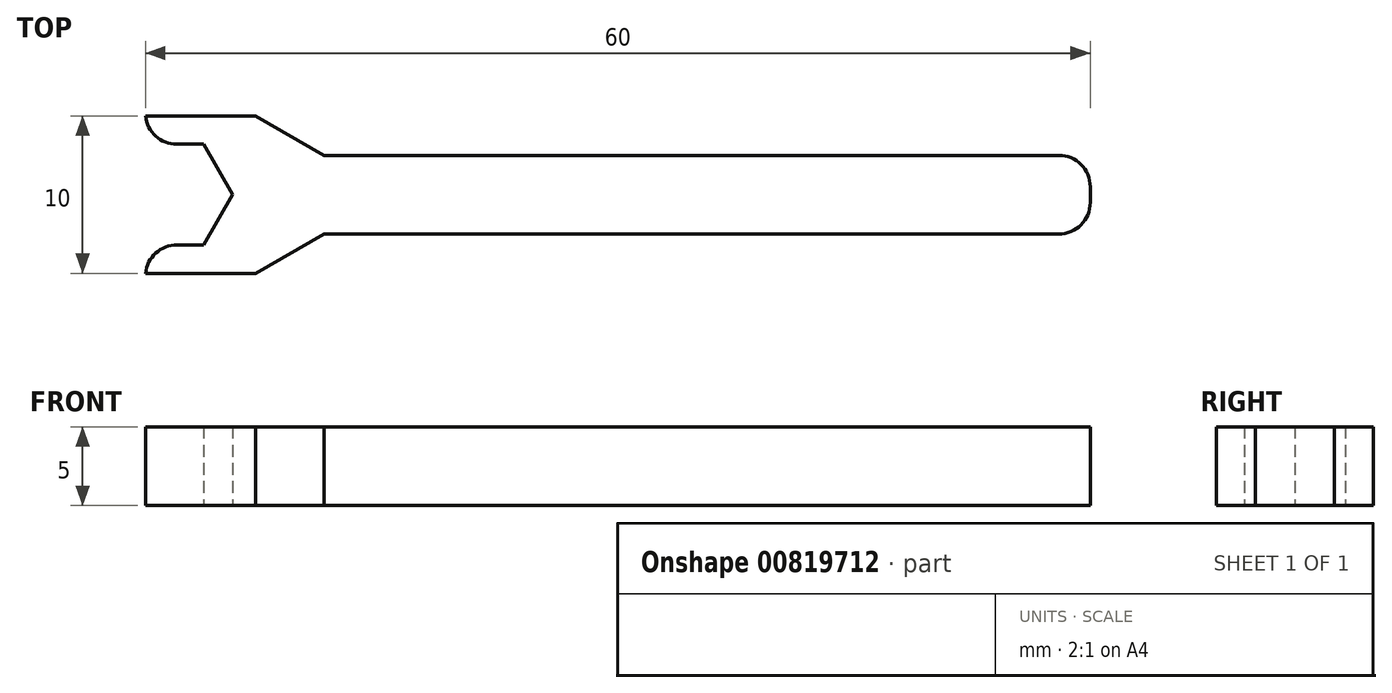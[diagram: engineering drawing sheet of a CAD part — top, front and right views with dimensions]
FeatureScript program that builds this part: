
annotation { "Feature Type Name" : "Feature", "Feature Type Description" : "" }
export const myFeature = defineFeature(function(context is Context, id is Id, definition is map)
    precondition{}
    {
        {
            var Q0;
            Q0=qCreatedBy(makeId("Top.planeOp"),FACE);
            var sketch = newSketch(context, id + "F0", { "sketchPlane" : qUnion([Q0])});
            skCircle(sketch, "E0.cCircle", {"center": v(0, 0) * mm, "radius": 3.2 * mm, "construction": true});
            skLineSegment(sketch, "E0.0", {"start": v(3.7, 0) * mm, "end": v(1.85, -3.2) * mm});
            skLineSegment(sketch, "E0.1", {"start": v(1.85, -3.2) * mm, "end": v(-1.85, -3.2) * mm});
            skLineSegment(sketch, "E0.2", {"start": v(-1.85, -3.2) * mm, "end": v(-3.7, 0) * mm, "construction": true});
            skLineSegment(sketch, "E0.3", {"start": v(-3.7, 0) * mm, "end": v(-1.85, 3.2) * mm, "construction": true});
            skLineSegment(sketch, "E0.4", {"start": v(-1.85, 3.2) * mm, "end": v(1.85, 3.2) * mm});
            skLineSegment(sketch, "E0.5", {"start": v(1.85, 3.2) * mm, "end": v(3.7, 0) * mm});
            skPoint(sketch, "E0.0.midPoint", {"position": v(2.77, -1.6) * mm});
            skLineSegment(sketch, "E1", {"start": v(-1.85, 3.2) * mm, "end": v(-1.85, 5) * mm});
            skLineSegment(sketch, "E2", {"start": v(-1.85, 5) * mm, "end": v(5.15, 5) * mm});
            skLineSegment(sketch, "E3", {"start": v(5.15, 5) * mm, "end": v(9.48, 2.5) * mm});
            skLineSegment(sketch, "E4", {"start": v(9.48, 2.5) * mm, "end": v(58.15, 2.5) * mm});
            skLineSegment(sketch, "E5", {"start": v(-4.42, 0) * mm, "end": v(61.3, 0) * mm, "construction": true});
            skLineSegment(sketch, "E6.MirrorCS", {"start": v(9.48, -2.5) * mm, "end": v(58.15, -2.5) * mm});
            skLineSegment(sketch, "E7.MirrorCS", {"start": v(-1.85, -5) * mm, "end": v(5.15, -5) * mm});
            skLineSegment(sketch, "E8.MirrorCS", {"start": v(-1.85, -3.2) * mm, "end": v(-1.85, -5) * mm});
            skLineSegment(sketch, "E9.MirrorCS", {"start": v(5.15, -5) * mm, "end": v(9.48, -2.5) * mm});
            skLineSegment(sketch, "E10", {"start": v(58.15, -2.5) * mm, "end": v(58.15, 2.5) * mm});
            skSolve(sketch);
        }
        {
            var Q0;
            Q0 = qSketchRegion(id + "F0", true);
            extrude(context, id + "F1", {"entities" : qUnion([Q0]), "endBound" : BoundingType.SYMMETRIC, "depth" : 5 * mm, "offsetDistance" : 25 * mm});
        }
        {
            var Q0;
            Q0=makeQuery(id+"F1.opExtrude","SWEPT_EDGE",EDGE,{"disambiguationData":[OSD([sQuery(id+"F0.wireOp",EDGE,"E0.4"),sQuery(id+"F0.wireOp",EDGE,"E1")])]});
            var Q1;
            Q1=makeQuery(id+"F1.opExtrude","SWEPT_EDGE",EDGE,{"disambiguationData":[OSD([sQuery(id+"F0.wireOp",EDGE,"E0.1"),sQuery(id+"F0.wireOp",EDGE,"E8.MirrorCS")])]});
            var Q2;
            Q2=makeQuery(id+"F1.opExtrude","SWEPT_EDGE",EDGE,{"disambiguationData":[OSD([sQuery(id+"F0.wireOp",EDGE,"E6.MirrorCS"),sQuery(id+"F0.wireOp",EDGE,"E10")])]});
            var Q3;
            Q3=makeQuery(id+"F1.opExtrude","SWEPT_EDGE",EDGE,{"disambiguationData":[OSD([sQuery(id+"F0.wireOp",EDGE,"E4"),sQuery(id+"F0.wireOp",EDGE,"E10")])]});
            fillet(context, id + "F2", {"entities" : qUnion([Q0, Q1, Q2, Q3]), "radius" : 2 * mm, "tangentPropagation" : true, "allowEdgeOverflow" : false});
        }
    });
